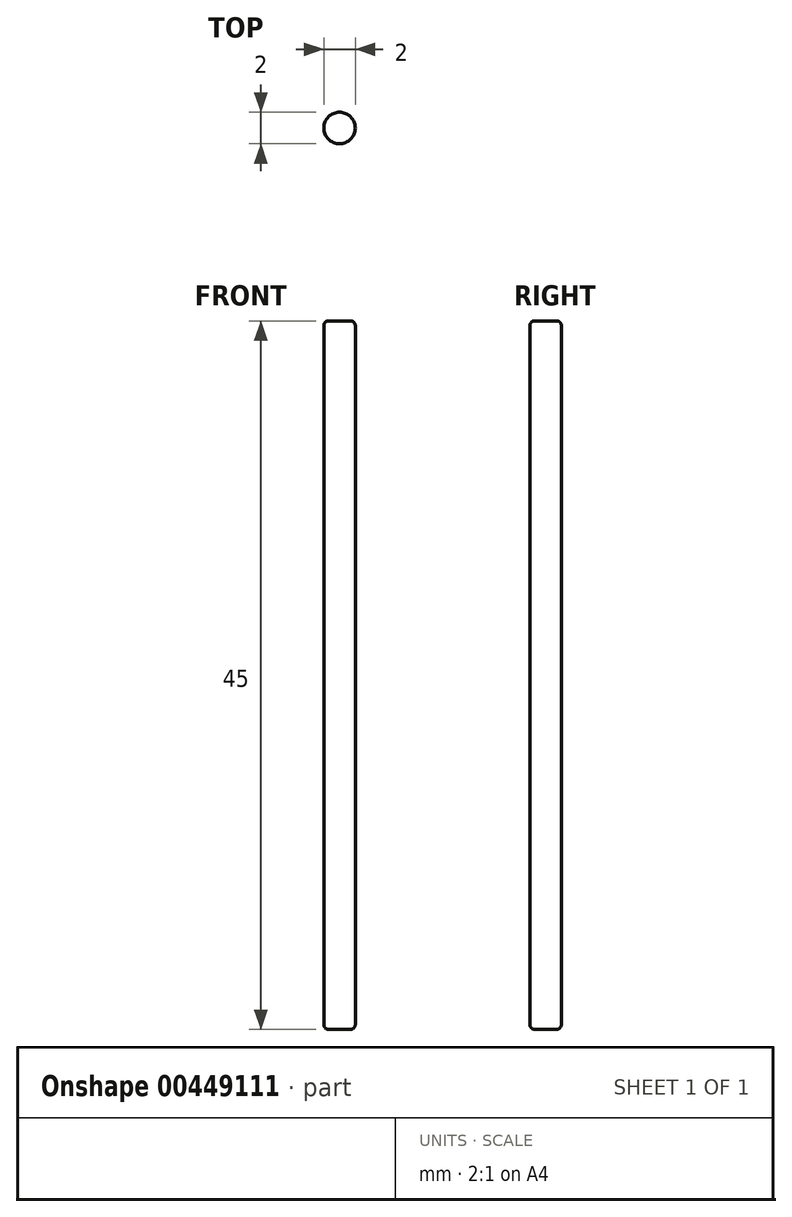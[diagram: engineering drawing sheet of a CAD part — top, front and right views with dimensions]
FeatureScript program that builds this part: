
annotation { "Feature Type Name" : "Feature", "Feature Type Description" : "" }
export const myFeature = defineFeature(function(context is Context, id is Id, definition is map)
    precondition{}
    {
        {
            var Q0;
            Q0=qCreatedBy(makeId("Top.planeOp"),FACE);
            var sketch = newSketch(context, id + "F0", { "sketchPlane" : qUnion([Q0])});
            skCircle(sketch, "E0", {"center": v(0, 0) * mm, "radius": 1 * mm});
            skSolve(sketch);
        }
        {
            var Q0;
            Q0=makeQuery(id+"F0.imprint","IMPRINT",FACE,{"disambiguationData":[TD([[makeQuery(id+"F0.imprint","IMPRINT",EDGE,{"derivedFrom":sQuery(id+"F0.wireOp",EDGE,"E0")}),1.0]])]});
            extrude(context, id + "F1", {"entities" : qUnion([Q0]), "depth" : (38 + 7) * mm});
        }
        {
            var Q0;
            Q0=makeQuery(id+"F1.opExtrude","CAP_EDGE",EDGE,{"disambiguationData":[OSD([sQuery(id+"F0.wireOp",EDGE,"E0")])],"isStart":false});
            fillet(context, id + "F2", {"entities" : qUnion([Q0]), "radius" : 0.3 * mm, "allowEdgeOverflow" : false});
        }
        {
            var Q0;
            Q0=makeQuery(id+"F1.opExtrude","CAP_EDGE",EDGE,{"disambiguationData":[OSD([sQuery(id+"F0.wireOp",EDGE,"E0")])],"isStart":true});
            fillet(context, id + "F3", {"entities" : qUnion([Q0]), "radius" : 0.3 * mm, "allowEdgeOverflow" : false});
        }
    });
